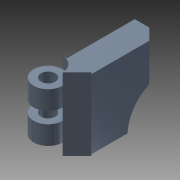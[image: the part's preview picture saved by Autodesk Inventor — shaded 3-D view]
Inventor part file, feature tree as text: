
AUTODESK INVENTOR PART (.ipt)
format: ipt  version: 2015 (Build 190159000, 159)  size: 184,832 bytes
history: native  units: mm
features: sketch x6, extrude x4, other x2, revolve x2, plane x1
ambient origin geometry x8: Origin, YZ Plane, XZ Plane, XY Plane, X Axis, Y Axis, Z Axis, Center Point
bodies: 实体1 (feature_tree)
feature tree (15):
  extrude  "拉伸1"  Depth=10.0mm
  plane  "工作平面1"
  other  "工作轴1"
  revolve  "旋转1"  [1 undecoded]
  extrude  "拉伸2"  Depth=10.0mm
  extrude  "拉伸3"  Depth=50.0mm TaperAngle=0.0deg
  extrude  "拉伸4"  Depth=14.0mm
  revolve  "旋转2"  Angle=90.0deg
  sketch  "草图1"  dims[d0=20.0mm d1=10.0mm]
  other  "工作点1"
  sketch  "草图3"  dims[d2=20.0mm d3=50.0mm]
  sketch  "草图4"  dims[d4=135.0deg d5=10.0mm]
  sketch  "草图5"  dims[d6=45.0deg d7=50.0mm d8=0.0mm]
  sketch  "草图6"  dims[d9=-25.0mm d13=14.0mm]
  sketch  "草图7"  dims[d14=25.0mm d15=90.0deg d16=2.0mm d17=2.0mm d18=50.0mm d19=0.0mm d20=1.0mm d21=1.0mm d22=48.0mm d23=0.0mm d24=50.0mm d25=2.0mm d26=20.0mm d27=0.0mm d28=8.0mm d29=13.0mm d30=21.0mm d31=13.0mm d32=8.0mm d33=10.0mm d34=10.0mm d35=10.0mm d36=90.0deg]
note: 1 required parameter value undecoded (feature->parameter linkage not recoverable at this tier; creation-order binding heuristic only, values carry confidence <= 0.55)
